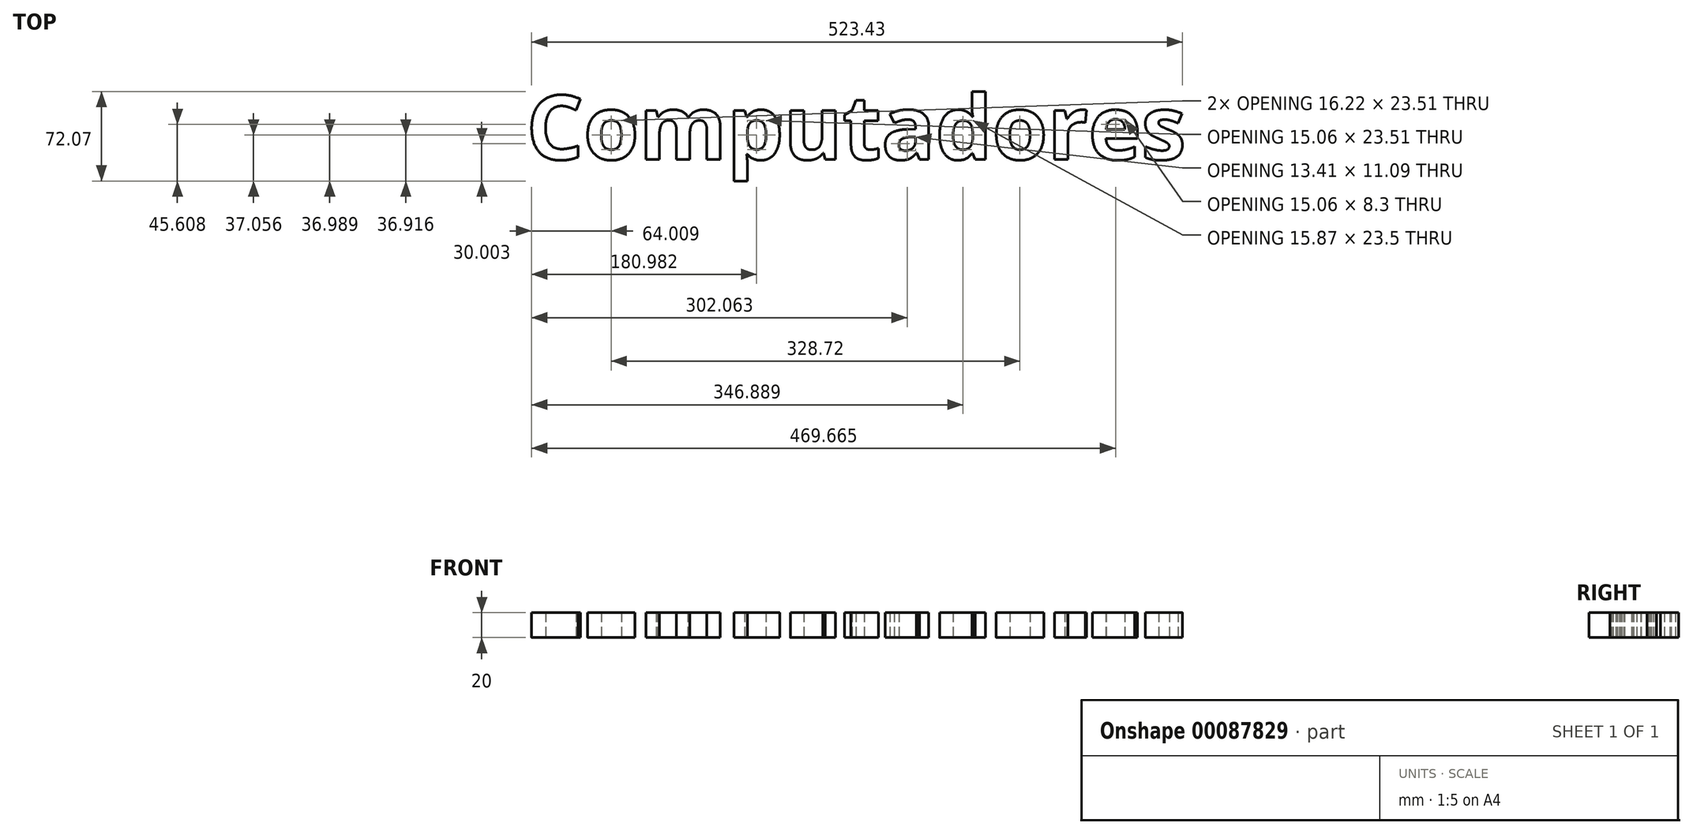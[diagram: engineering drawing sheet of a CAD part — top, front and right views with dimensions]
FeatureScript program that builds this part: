
annotation { "Feature Type Name" : "Feature", "Feature Type Description" : "" }
export const myFeature = defineFeature(function(context is Context, id is Id, definition is map)
    precondition{}
    {
        {
            var Q0;
            Q0=qCreatedBy(makeId("Top.planeOp"),FACE);
            var sketch = newSketch(context, id + "F0", { "sketchPlane" : qUnion([Q0])});
            skText(sketch, "E0", { "text": "Computadores", "fontName": "OpenSans-Bold.ttf"});
            const initialGuessF0  = {"E0": [-0.04947, -0.02143, 1, 0, 0.05188]};
            skSetInitialGuess(sketch, initialGuessF0);
            skSolve(sketch);
        }
        {
            var Q0;
            Q0 = qSketchRegion(id + "F0", true);
            extrude(context, id + "F1", {"entities" : qUnion([Q0]), "endBound" : BoundingType.SYMMETRIC, "depth" : 20 * mm});
        }
    });
